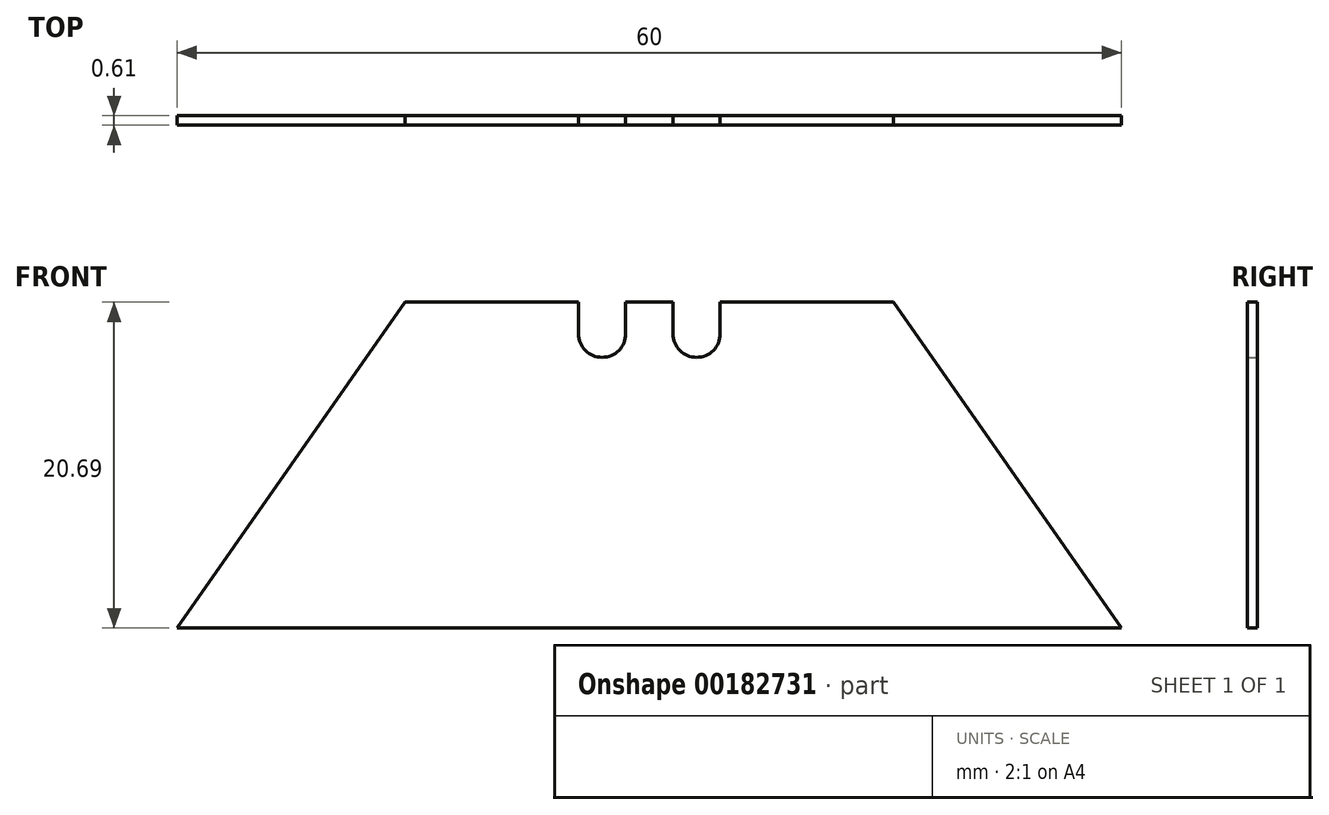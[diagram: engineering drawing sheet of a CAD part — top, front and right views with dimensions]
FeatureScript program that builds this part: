
annotation { "Feature Type Name" : "Feature", "Feature Type Description" : "" }
export const myFeature = defineFeature(function(context is Context, id is Id, definition is map)
    precondition{}
    {
        {
            var Q0;
            Q0=qCreatedBy(makeId("Front.planeOp"),FACE);
            var sketch = newSketch(context, id + "F0", { "sketchPlane" : qUnion([Q0])});
            skLineSegment(sketch, "E0", {"start": v(0, 0) * mm, "end": v(-30, 0) * mm});
            skLineSegment(sketch, "E1", {"start": v(0, 0) * mm, "end": v(30, 0) * mm});
            skLineSegment(sketch, "E2", {"start": v(0, 20.69) * mm, "end": v(-1.5, 20.69) * mm});
            skLineSegment(sketch, "E3", {"start": v(0, 20.69) * mm, "end": v(1.5, 20.69) * mm});
            skLineSegment(sketch, "E4", {"start": v(-4.5, 20.69) * mm, "end": v(-15.5, 20.69) * mm});
            skLineSegment(sketch, "E5", {"start": v(-15.5, 20.69) * mm, "end": v(-30, 0) * mm});
            skLineSegment(sketch, "E6", {"start": v(4.5, 20.69) * mm, "end": v(15.5, 20.69) * mm});
            skLineSegment(sketch, "E7", {"start": v(15.5, 20.69) * mm, "end": v(30, 0) * mm});
            skLineSegment(sketch, "E8", {"start": v(-4.5, 20.69) * mm, "end": v(-4.5, 18.69) * mm});
            skLineSegment(sketch, "E9", {"start": v(-1.5, 20.69) * mm, "end": v(-1.5, 18.69) * mm});
            skLineSegment(sketch, "E10", {"start": v(1.5, 20.69) * mm, "end": v(1.5, 18.69) * mm});
            skLineSegment(sketch, "E11", {"start": v(4.5, 20.69) * mm, "end": v(4.5, 18.69) * mm});
            skArc(sketch, "E12", {"start": v(-1.5, 18.69) * mm, "mid": v(-3, 17.19) * mm, "end": v(-4.5, 18.69) * mm});
            skArc(sketch, "E13", {"start": v(4.5, 18.69) * mm, "mid": v(3, 17.19) * mm, "end": v(1.5, 18.69) * mm});
            skSolve(sketch);
        }
        {
            var Q0;
            Q0=makeQuery(id+"F0.imprint","IMPRINT",FACE,{"disambiguationData":[TD([[makeQuery(id+"F0.imprint","IMPRINT",EDGE,{"derivedFrom":sQuery(id+"F0.wireOp",EDGE,"E0")}),-1.0]])]});
            extrude(context, id + "F1", {"entities" : qUnion([Q0]), "depth" : 0.61 * mm});
        }
    });
